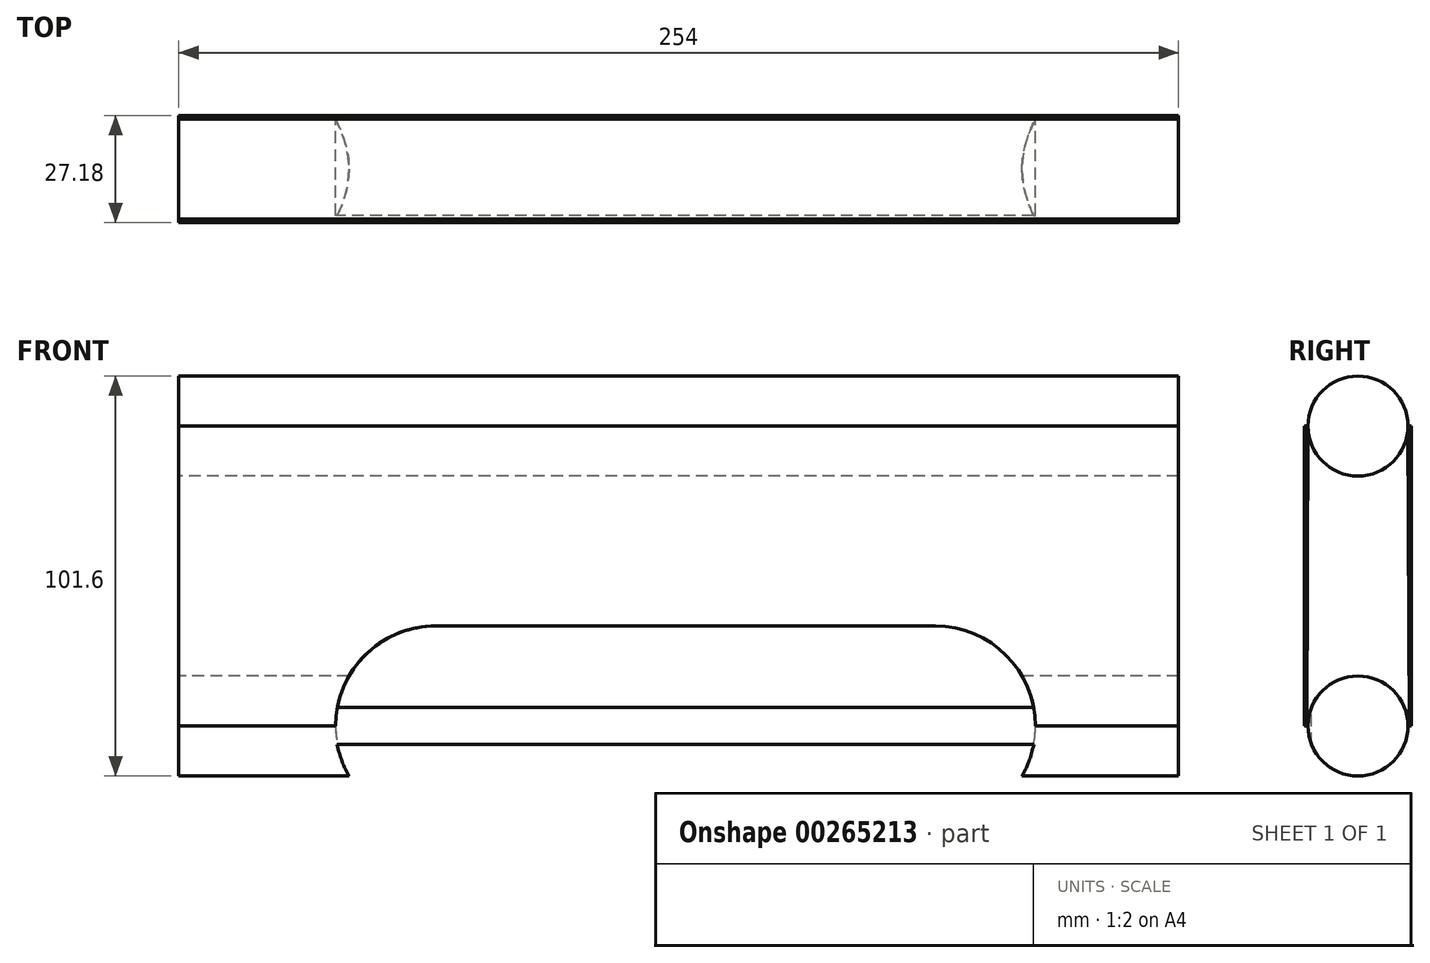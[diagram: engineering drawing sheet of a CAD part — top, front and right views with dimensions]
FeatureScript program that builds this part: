
annotation { "Feature Type Name" : "Feature", "Feature Type Description" : "" }
export const myFeature = defineFeature(function(context is Context, id is Id, definition is map)
    precondition{}
    {
        {
            var Q0;
            Q0=qCreatedBy(makeId("Right.planeOp"),FACE);
            var sketch = newSketch(context, id + "F0", { "sketchPlane" : qUnion([Q0])});
            skCircle(sketch, "E0", {"center": v(0, 38.1) * mm, "radius": 12.7 * mm});
            skCircle(sketch, "E1", {"center": v(0, -38.1) * mm, "radius": 12.7 * mm});
            skLineSegment(sketch, "E2", {"start": v(0, 38.1) * mm, "end": v(0, -38.1) * mm, "construction": true});
            skSolve(sketch);
        }
        {
            var Q0;
            Q0 = qSketchRegion(id + "F0", true);
            extrude(context, id + "F1", {"entities" : qUnion([Q0]), "endBound" : BoundingType.SYMMETRIC, "depth" : 254 * mm});
        }
        {
            var Q0;
            Q0=makeQuery(id+"F1.opExtrude","CAP_FACE",FACE,{"disambiguationData":[OSD([sQuery(id+"F0.wireOp",EDGE,"E0")])],"isStart":false});
            var sketch = newSketch(context, id + "F2", { "sketchPlane" : qUnion([Q0])});
            skLineSegment(sketch, "E3", {"start": v(12.7, 38.1) * mm, "end": v(13.59, 38.1) * mm});
            skLineSegment(sketch, "E4", {"start": v(13.59, 38.1) * mm, "end": v(13.59, -38.1) * mm});
            skLineSegment(sketch, "E5", {"start": v(13.59, -38.1) * mm, "end": v(13, -38.1) * mm});
            skLineSegment(sketch, "E6", {"start": v(13, -38.1) * mm, "end": v(12.7, 38.1) * mm});
            skPoint(sketch, "E7", {"position": v(0, 38.1) * mm});
            skPoint(sketch, "E8", {"position": v(0, -38.1) * mm});
            skSolve(sketch);
        }
        {
            var Q0;
            Q0 = qSketchRegion(id + "F2", true);
            var Q1;
            Q1=makeQuery(id+"F1.opExtrude","CAP_FACE",FACE,{"disambiguationData":[OSD([sQuery(id+"F0.wireOp",EDGE,"E0")])],"isStart":true});
            extrude(context, id + "F3", {"entities" : qUnion([Q0]), "endBound" : BoundingType.UP_TO_SURFACE, "oppositeDirection" : true, "endBoundEntityFace" : qUnion([Q1]), "depth" : 25.4 * mm});
        }
        {
            var Q0;
            Q0=makeQuery(id+"F3.opExtrude","SWEPT_FACE",FACE,{"disambiguationData":[OSD([sQuery(id+"F2.wireOp",EDGE,"E4")])]});
            var sketch = newSketch(context, id + "F4", { "sketchPlane" : qUnion([Q0])});
            skArc(sketch, "E9", {"start": v(-65.24, -12.7) * mm, "mid": v(-90.64, -38.1) * mm, "end": v(-65.24, -63.5) * mm});
            skArc(sketch, "E10", {"start": v(61.76, -63.5) * mm, "mid": v(87.16, -38.1) * mm, "end": v(61.76, -12.7) * mm});
            skLineSegment(sketch, "E11", {"start": v(-65.24, -12.7) * mm, "end": v(61.76, -12.7) * mm});
            skLineSegment(sketch, "E12", {"start": v(-65.24, -63.5) * mm, "end": v(61.76, -63.5) * mm});
            skSolve(sketch);
        }
        {
            var Q0;
            Q0 = qSketchRegion(id + "F4", true);
            extrude(context, id + "F5", {"entities" : qUnion([Q0]), "operationType" : NewBodyOperationType.REMOVE, "oppositeDirection" : true, "depth" : 25.4 * mm});
        }
        {
            var Q0;
            Q0=makeQuery(id+"F3.opExtrude","SWEPT_BODY",BODY,{"disambiguationData":[OSD([sQuery(id+"F2.wireOp",EDGE,"E3"),sQuery(id+"F2.wireOp",EDGE,"E4"),sQuery(id+"F2.wireOp",EDGE,"E5"),sQuery(id+"F2.wireOp",EDGE,"E6")])]});
            var Q1;
            Q1=qCreatedBy(makeId("Front.planeOp"),FACE);
            mirror(context, id + "F6", {"entities" : qUnion([Q0]), "mirrorPlane" : qUnion([Q1])});
        }
    });
